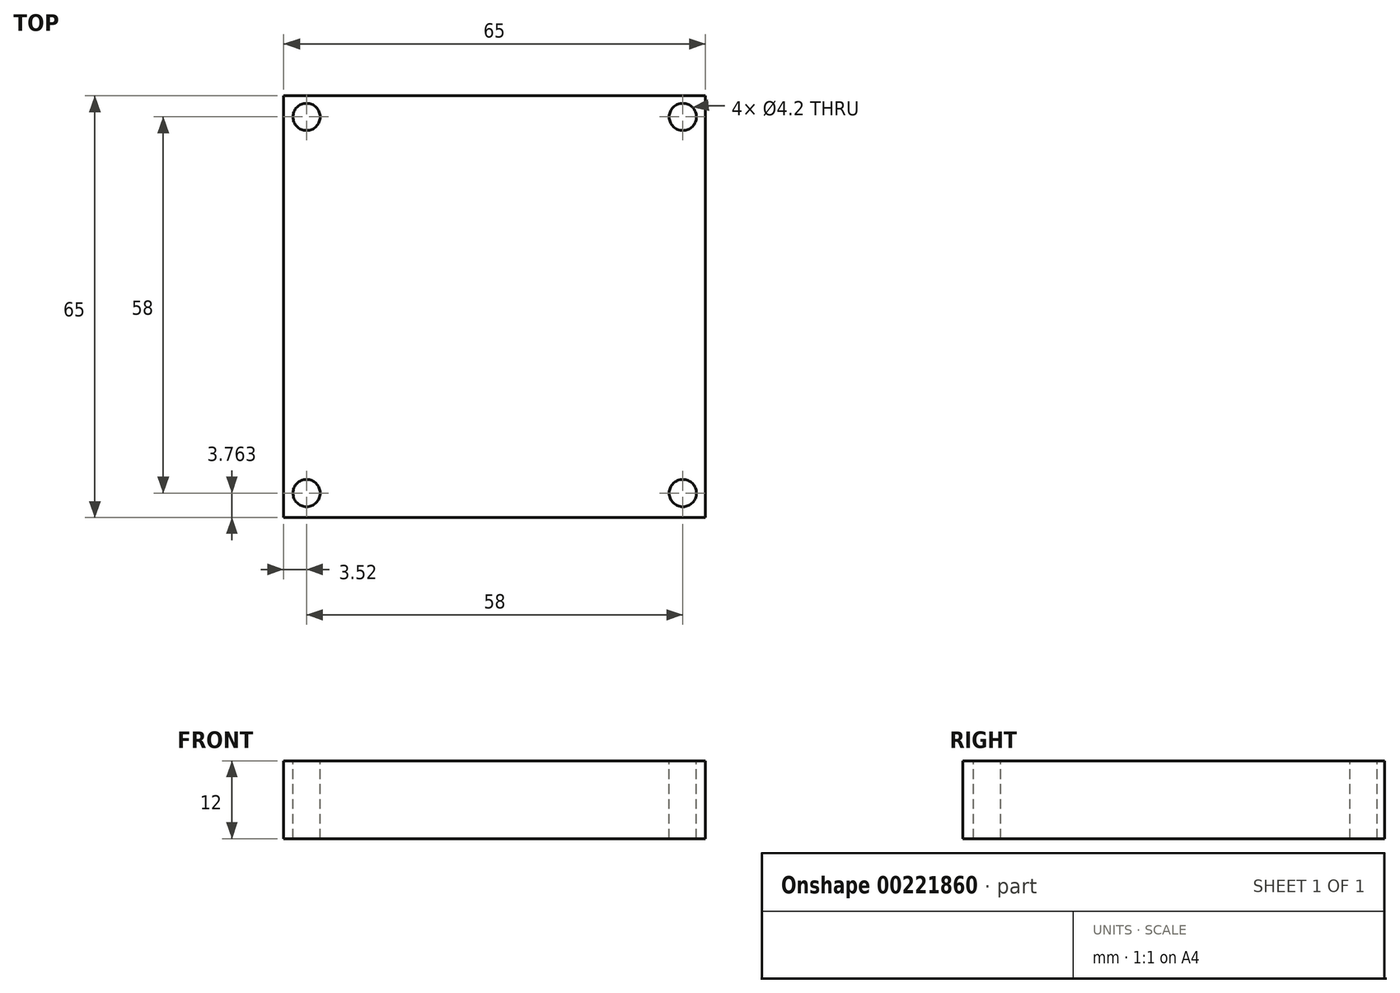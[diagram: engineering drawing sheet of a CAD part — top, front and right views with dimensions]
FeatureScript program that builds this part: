
annotation { "Feature Type Name" : "Feature", "Feature Type Description" : "" }
export const myFeature = defineFeature(function(context is Context, id is Id, definition is map)
    precondition{}
    {
        {
            var Q0;
            Q0=qCreatedBy(makeId("Top.planeOp"),FACE);
            var sketch = newSketch(context, id + "F0", { "sketchPlane" : qUnion([Q0])});
            skLineSegment(sketch, "E0.bottom", {"start": v(-32.5, 32.5) * mm, "end": v(32.5, 32.5) * mm});
            skLineSegment(sketch, "E0.top", {"start": v(-32.5, -32.5) * mm, "end": v(32.5, -32.5) * mm});
            skLineSegment(sketch, "E0.left", {"start": v(-32.5, 32.5) * mm, "end": v(-32.5, -32.5) * mm});
            skLineSegment(sketch, "E0.right", {"start": v(32.5, 32.5) * mm, "end": v(32.5, -32.5) * mm});
            skPoint(sketch, "E0.middle", {"position": v(0, 0) * mm});
            skSolve(sketch);
        }
        {
            var Q0;
            Q0=makeQuery(id+"F0.imprint","IMPRINT",FACE,{"disambiguationData":[TD([[makeQuery(id+"F0.imprint","IMPRINT",EDGE,{"derivedFrom":sQuery(id+"F0.wireOp",EDGE,"E0.bottom")}),-1.0]])]});
            extrude(context, id + "F1", {"entities" : qUnion([Q0]), "depth" : 7 * mm});
        }
        {
            var Q0;
            Q0=makeQuery(id+"F1.opExtrude","CAP_FACE",FACE,{"disambiguationData":[OSD([sQuery(id+"F0.wireOp",EDGE,"E0.bottom"),sQuery(id+"F0.wireOp",EDGE,"E0.top"),sQuery(id+"F0.wireOp",EDGE,"E0.left"),sQuery(id+"F0.wireOp",EDGE,"E0.right")])],"isStart":true});
            var sketch = newSketch(context, id + "F2", { "sketchPlane" : qUnion([Q0])});
            skLineSegment(sketch, "E1.bottom", {"start": v(-32.5, 32.5) * mm, "end": v(32.5, 32.5) * mm});
            skLineSegment(sketch, "E1.top", {"start": v(-32.5, -32.5) * mm, "end": v(32.5, -32.5) * mm});
            skLineSegment(sketch, "E1.left", {"start": v(-32.5, 32.5) * mm, "end": v(-32.5, -32.5) * mm});
            skLineSegment(sketch, "E1.right", {"start": v(32.5, 32.5) * mm, "end": v(32.5, -32.5) * mm});
            skPoint(sketch, "E1.middle", {"position": v(0, 0) * mm});
            skSolve(sketch);
        }
        {
            var Q0;
            Q0=qSketchRegion(id+"F2",true);
            extrude(context, id + "F3", {"entities" : qUnion([Q0]), "operationType" : NewBodyOperationType.ADD, "depth" : 5 * mm});
        }
        {
            var Q0;
            Q0=makeQuery(id+"F1.opExtrude","CAP_FACE",FACE,{"disambiguationData":[OSD([sQuery(id+"F0.wireOp",EDGE,"E0.bottom"),sQuery(id+"F0.wireOp",EDGE,"E0.top"),sQuery(id+"F0.wireOp",EDGE,"E0.left"),sQuery(id+"F0.wireOp",EDGE,"E0.right")])],"isStart":false});
            var sketch = newSketch(context, id + "F4", { "sketchPlane" : qUnion([Q0])});
            skCircle(sketch, "E2", {"center": v(-28.98, 29.26) * mm, "radius": 2.1 * mm});
            skCircle(sketch, "E3", {"center": v(-28.98, -28.74) * mm, "radius": 2.1 * mm});
            skCircle(sketch, "E4", {"center": v(29.02, -28.74) * mm, "radius": 2.1 * mm});
            skCircle(sketch, "E5", {"center": v(29.02, 29.26) * mm, "radius": 2.1 * mm});
            skSolve(sketch);
        }
        {
            var Q0;
            Q0=makeQuery(id+"F4.imprint","IMPRINT",FACE,{"disambiguationData":[TD([[makeQuery(id+"F4.imprint","IMPRINT",EDGE,{"derivedFrom":sQuery(id+"F4.wireOp",EDGE,"E2")}),1.0]])]});
            var Q1;
            Q1=makeQuery(id+"F4.imprint","IMPRINT",FACE,{"disambiguationData":[TD([[makeQuery(id+"F4.imprint","IMPRINT",EDGE,{"derivedFrom":sQuery(id+"F4.wireOp",EDGE,"E5")}),1.0]])]});
            var Q2;
            Q2=makeQuery(id+"F4.imprint","IMPRINT",FACE,{"disambiguationData":[TD([[makeQuery(id+"F4.imprint","IMPRINT",EDGE,{"derivedFrom":sQuery(id+"F4.wireOp",EDGE,"E4")}),1.0]])]});
            var Q3;
            Q3=makeQuery(id+"F4.imprint","IMPRINT",FACE,{"disambiguationData":[TD([[makeQuery(id+"F4.imprint","IMPRINT",EDGE,{"derivedFrom":sQuery(id+"F4.wireOp",EDGE,"E3")}),1.0]])]});
            extrude(context, id + "F5", {"entities" : qUnion([Q0, Q1, Q2, Q3]), "operationType" : NewBodyOperationType.REMOVE, "oppositeDirection" : true, "depth" : 39 * mm});
        }
    });
